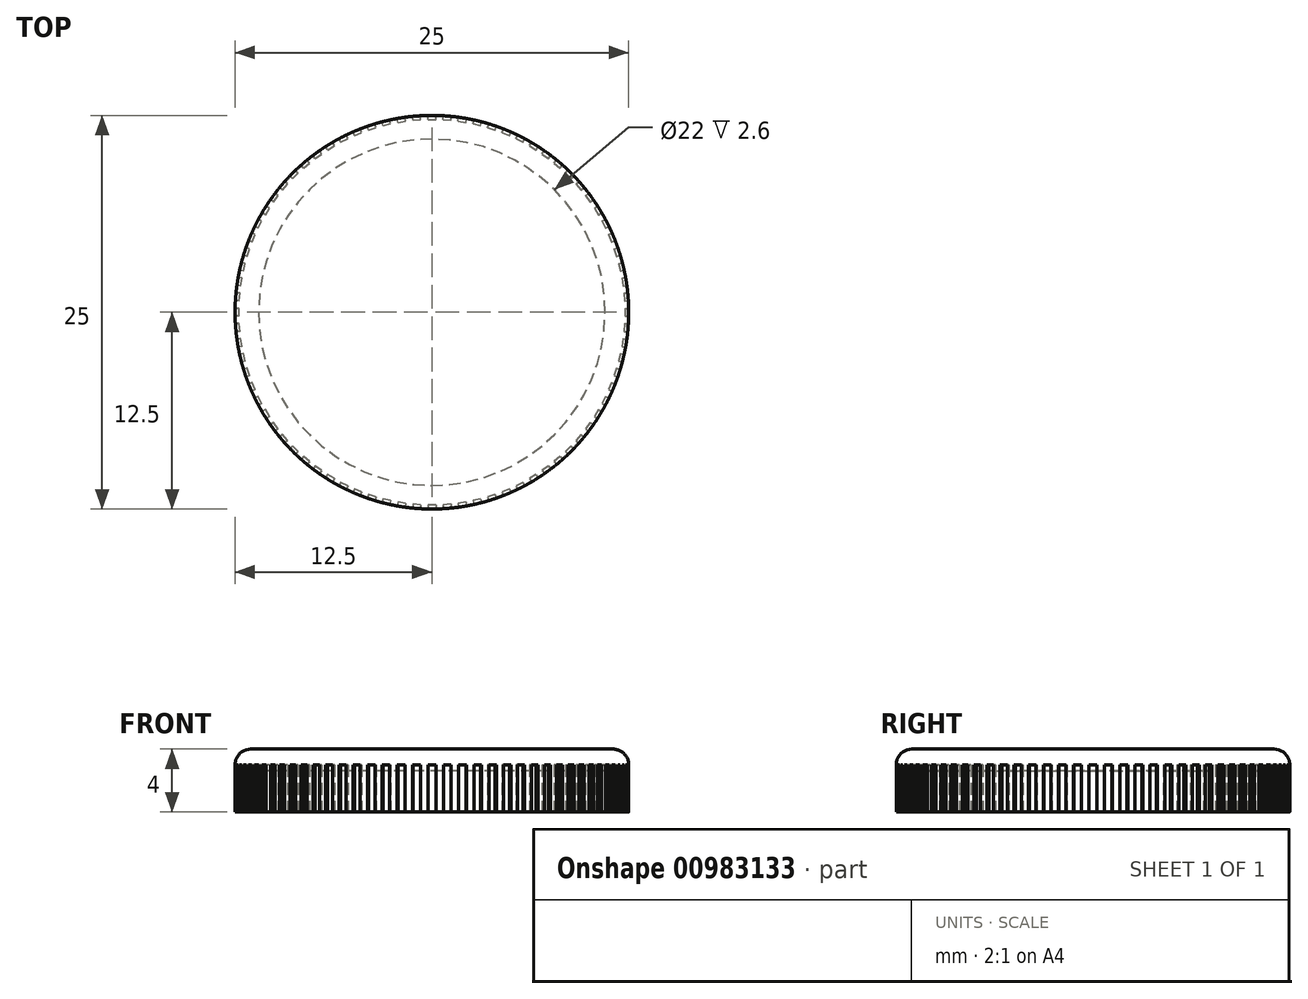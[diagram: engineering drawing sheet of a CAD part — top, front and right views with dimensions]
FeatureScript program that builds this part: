
annotation { "Feature Type Name" : "Feature", "Feature Type Description" : "" }
export const myFeature = defineFeature(function(context is Context, id is Id, definition is map)
    precondition{}
    {
        {
            var Q0;
            Q0=qCreatedBy(makeId("Top.planeOp"),FACE);
            var sketch = newSketch(context, id + "F0", { "sketchPlane" : qUnion([Q0])});
            skCircle(sketch, "E0", {"center": v(0, 0) * mm, "radius": 11 * mm});
            skCircle(sketch, "E1", {"center": v(0, 0) * mm, "radius": 12.5 * mm});
            skSolve(sketch);
        }
        {
            var Q0;
            Q0=makeQuery(id+"F0.imprint","IMPRINT",FACE,{"disambiguationData":[TD([[makeQuery(id+"F0.imprint","IMPRINT",EDGE,{"derivedFrom":sQuery(id+"F0.wireOp",EDGE,"E0")}),-1.0]])]});
            var Q1;
            Q1=makeQuery(id+"F0.imprint","IMPRINT",FACE,{"disambiguationData":[TD([[makeQuery(id+"F0.imprint","IMPRINT",EDGE,{"derivedFrom":sQuery(id+"F0.wireOp",EDGE,"E0")}),1.0]])]});
            extrude(context, id + "F1", {"entities" : qUnion([Q0, Q1]), "depth" : 4 * mm, "offsetDistance" : 25 * mm});
        }
        {
            var Q0;
            Q0=makeQuery(id+"F0.imprint","IMPRINT",FACE,{"disambiguationData":[TD([[makeQuery(id+"F0.imprint","IMPRINT",EDGE,{"derivedFrom":sQuery(id+"F0.wireOp",EDGE,"E0")}),1.0]])]});
            extrude(context, id + "F2", {"entities" : qUnion([Q0]), "operationType" : NewBodyOperationType.REMOVE, "depth" : 2.6 * mm, "offsetDistance" : 25 * mm});
        }
        {
            var Q0;
            Q0=makeQuery(id+"F1.opExtrude","CAP_EDGE",EDGE,{"disambiguationData":[OSD([sQuery(id+"F0.wireOp",EDGE,"E1")])],"isStart":false});
            fillet(context, id + "F3", {"entities" : qUnion([Q0]), "radius" : 1 * mm, "tangentPropagation" : true, "allowEdgeOverflow" : false});
        }
        {
            var Q0;
            Q0=makeQuery(id+"F1.opExtrude","CAP_FACE",FACE,{"disambiguationData":[OSD([sQuery(id+"F0.wireOp",EDGE,"E1")])],"isStart":true});
            var sketch = newSketch(context, id + "F4", { "sketchPlane" : qUnion([Q0])});
            skLineSegment(sketch, "E2.bottom", {"start": v(0.25, 12.25) * mm, "end": v(-0.25, 12.25) * mm});
            skLineSegment(sketch, "E2.top", {"start": v(0.25, 12.75) * mm, "end": v(-0.25, 12.75) * mm});
            skLineSegment(sketch, "E2.left", {"start": v(0.25, 12.25) * mm, "end": v(0.25, 12.75) * mm});
            skLineSegment(sketch, "E2.right", {"start": v(-0.25, 12.25) * mm, "end": v(-0.25, 12.75) * mm});
            skPoint(sketch, "E2.middle", {"position": v(0, 12.5) * mm});
            skSolve(sketch);
        }
        {
            var Q0;
            Q0 = qSketchRegion(id + "F4", true);
            extrude(context, id + "F5", {"entities" : qUnion([Q0]), "oppositeDirection" : true, "depth" : 3 * mm, "offsetDistance" : 25 * mm});
        }
        {
            var Q0;
            Q0=makeQuery(id+"F5.opExtrude","SWEPT_BODY",BODY,{"disambiguationData":[OSD([sQuery(id+"F4.wireOp",EDGE,"E2.bottom"),sQuery(id+"F4.wireOp",EDGE,"E2.top"),sQuery(id+"F4.wireOp",EDGE,"E2.left"),sQuery(id+"F4.wireOp",EDGE,"E2.right")])]});
            var Q1;
            Q1=makeQuery(id+"F1.opExtrude","CAP_EDGE",EDGE,{"disambiguationData":[OSD([sQuery(id+"F0.wireOp",EDGE,"E1")])],"isStart":true});
            circularPattern(context, id + "F6", {"operationType" : NewBodyOperationType.REMOVE, "entities" : qUnion([Q0]), "axis" : qUnion([Q1]), "angle" : 360 * degree, "instanceCount" : 80, "equalSpace" : true, "computeTransformsWithoutBuiltin" : true});
        }
    });
